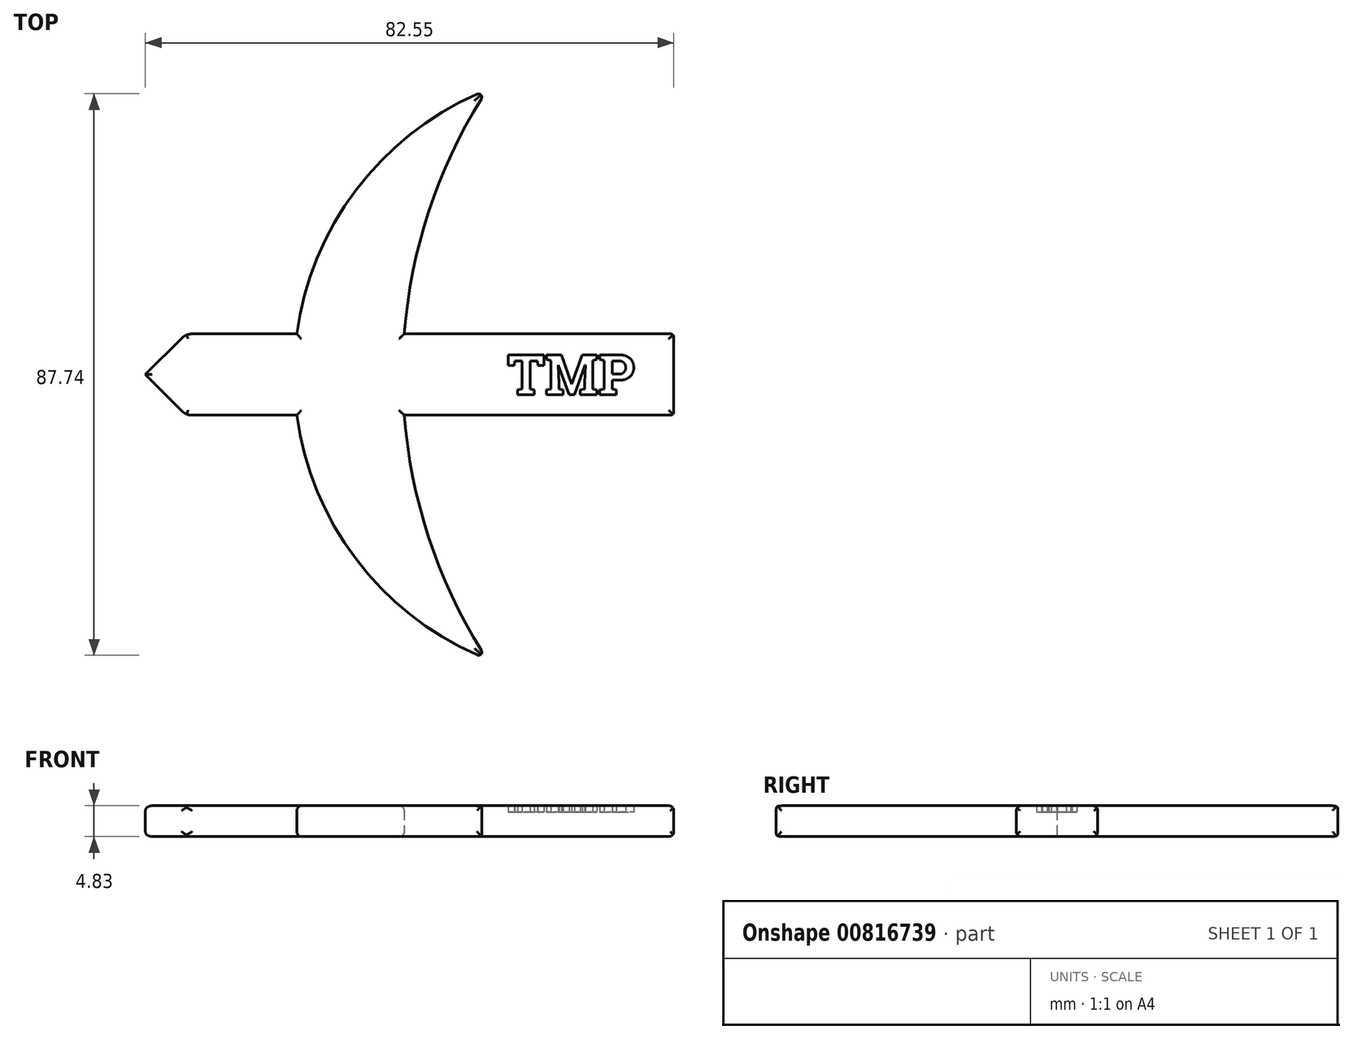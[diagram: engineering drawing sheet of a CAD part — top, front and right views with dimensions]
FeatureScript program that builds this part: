
annotation { "Feature Type Name" : "Feature", "Feature Type Description" : "" }
export const myFeature = defineFeature(function(context is Context, id is Id, definition is map)
    precondition{}
    {
        {
            var Q0;
            Q0=qCreatedBy(makeId("Top.planeOp"),FACE);
            var sketch = newSketch(context, id + "F0", { "sketchPlane" : qUnion([Q0])});
            skArc(sketch, "E0", {"start": v(0, 44.45) * mm, "mid": v(-30.1, 0) * mm, "end": v(0, -44.45) * mm});
            skArc(sketch, "E1", {"start": v(0, 44.45) * mm, "mid": v(-13.15, 0) * mm, "end": v(0, -44.45) * mm});
            skLineSegment(sketch, "E2", {"start": v(0, 0) * mm, "end": v(17.78, 0) * mm, "construction": true});
            skLineSegment(sketch, "E3", {"start": v(17.78, 0) * mm, "end": v(68.58, 0) * mm, "construction": true});
            skLineSegment(sketch, "E4.bottom", {"start": v(-47, 6.35) * mm, "end": v(29.2, 6.35) * mm});
            skLineSegment(sketch, "E4.top", {"start": v(-47, -6.35) * mm, "end": v(29.2, -6.35) * mm});
            skLineSegment(sketch, "E4.right", {"start": v(29.2, 6.35) * mm, "end": v(29.21, -6.35) * mm});
            skPoint(sketch, "E5", {"position": v(0, 0) * mm});
            skPoint(sketch, "E6", {"position": v(-8.9, 0) * mm});
            skLineSegment(sketch, "E7", {"start": v(-8.9, 6.35) * mm, "end": v(-8.9, -6.35) * mm, "construction": true});
            skLineSegment(sketch, "E8", {"start": v(-47, 6.35) * mm, "end": v(-53.34, 0) * mm});
            skLineSegment(sketch, "E9", {"start": v(-53.34, 0) * mm, "end": v(-47, -6.35) * mm});
            skSolve(sketch);
        }
        {
            var Q0;
            Q0 = qSketchRegion(id + "F0", true);
            extrude(context, id + "F1", {"entities" : qUnion([Q0]), "depth" : 4.83 * mm, "offsetDistance" : 25.4 * mm});
        }
        {
            var Q0;
            Q0=makeQuery(id+"F1.opExtrude","CAP_FACE",FACE,{"disambiguationData":[OSD([sQuery(id+"F0.wireOp",EDGE,"E0"),sQuery(id+"F0.wireOp",EDGE,"E1"),sQuery(id+"F0.wireOp",EDGE,"E4.bottom"),sQuery(id+"F0.wireOp",EDGE,"E4.top"),sQuery(id+"F0.wireOp",EDGE,"E4.right"),sQuery(id+"F0.wireOp",EDGE,"E8"),sQuery(id+"F0.wireOp",EDGE,"E9")])],"isStart":false});
            var Q1;
            Q1=makeQuery(id+"F1.opExtrude","CAP_FACE",FACE,{"disambiguationData":[OSD([sQuery(id+"F0.wireOp",EDGE,"E0"),sQuery(id+"F0.wireOp",EDGE,"E1"),sQuery(id+"F0.wireOp",EDGE,"E4.bottom"),sQuery(id+"F0.wireOp",EDGE,"E4.top"),sQuery(id+"F0.wireOp",EDGE,"E4.right"),sQuery(id+"F0.wireOp",EDGE,"E8"),sQuery(id+"F0.wireOp",EDGE,"E9")])],"isStart":true});
            fillet(context, id + "F2", {"entities" : qUnion([Q0, Q1]), "radius" : 0.76 * mm, "tangentPropagation" : true, "allowEdgeOverflow" : false});
        }
        {
            var Q0;
            Q0=makeQuery(id+"F1.opExtrude","SWEPT_EDGE",EDGE,{"disambiguationData":[OSD([sQuery(id+"F0.wireOp",EDGE,"E4.top"),sQuery(id+"F0.wireOp",EDGE,"E9")])]});
            var Q1;
            Q1=makeQuery(id+"F1.opExtrude","SWEPT_EDGE",EDGE,{"disambiguationData":[OSD([sQuery(id+"F0.wireOp",EDGE,"E4.bottom"),sQuery(id+"F0.wireOp",EDGE,"E8")])]});
            fillet(context, id + "F3", {"entities" : qUnion([Q0, Q1]), "radius" : 2.3 * mm, "allowEdgeOverflow" : false});
        }
        {
            var Q0;
            {var subQ0=sQuery(id+"F0.wireOp",EDGE,"E1");var subQ1=sQuery(id+"F0.wireOp",EDGE,"E0");Q0=makeQuery(id+"F1.opExtrude","SWEPT_EDGE",EDGE,{"disambiguationData":[OSD([subQ1,subQ0]),TDD([makeQuery(id+"F0.imprint","INTERSECT",VERTEX,{"disambiguationData":[OD(0.0)],"derivedFrom":[subQ1,subQ0]})])]});}
            var Q1;
            {var subQ0=sQuery(id+"F0.wireOp",EDGE,"E1");var subQ1=sQuery(id+"F0.wireOp",EDGE,"E0");Q1=makeQuery(id+"F1.opExtrude","SWEPT_EDGE",EDGE,{"disambiguationData":[OSD([subQ1,subQ0]),TDD([makeQuery(id+"F0.imprint","INTERSECT",VERTEX,{"disambiguationData":[OD(1.0)],"derivedFrom":[subQ1,subQ0]})])]});}
            var Q2;
            Q2=makeQuery(id+"F1.opExtrude","SWEPT_EDGE",EDGE,{"disambiguationData":[OSD([sQuery(id+"F0.wireOp",EDGE,"E4.top"),sQuery(id+"F0.wireOp",EDGE,"E4.right")])]});
            var Q3;
            Q3=makeQuery(id+"F1.opExtrude","SWEPT_EDGE",EDGE,{"disambiguationData":[OSD([sQuery(id+"F0.wireOp",EDGE,"E4.bottom"),sQuery(id+"F0.wireOp",EDGE,"E4.right")])]});
            fillet(context, id + "F4", {"entities" : qUnion([Q0, Q1, Q2, Q3]), "radius" : 0.5 * mm, "allowEdgeOverflow" : false});
        }
        {
            var Q0;
            Q0=qCreatedBy(makeId("Top.planeOp"),FACE);
            var sketch = newSketch(context, id + "F5", { "sketchPlane" : qUnion([Q0])});
            skText(sketch, "E10", { "text": "TMP", "fontName": "RobotoSlab-Bold.ttf"});
            skLineSegment(sketch, "E11", {"start": v(0, 0) * mm, "end": v(3.17, 0) * mm});
            const initialGuessF5  = {"E10": [0.00317, -0.00317, 1, 0, 0.00635]};
            skSetInitialGuess(sketch, initialGuessF5);
            skSolve(sketch);
        }
        {
            var Q0;
            Q0 = qSketchRegion(id + "F5", true);
            extrude(context, id + "F6", {"entities" : qUnion([Q0]), "operationType" : NewBodyOperationType.REMOVE, "depth" : 25.4 * mm, "offsetDistance" : 25.4 * mm, "hasSecondDirection" : true, "secondDirectionOppositeDirection" : false, "secondDirectionDepth" : 3.8 * mm});
        }
    });
